# Revit family: 208_S-_ ilmanvaihdon poisto
name_source: partatom
category: Air Terminals
units: mm (PartAtom-declared; Revit-internal decimal feet)

## family parameters
Always vertical = Yes
Cut with Voids When Loaded = No
Part Type = Normal
Room Calculation Point = Yes
Round Connector Dimension = Use Diameter
Shared = No
Work Plane-Based = No

## types (3) — shared parameters
CAT0 = Yes
CL_Location_5000 = 5000 mm  [stored 16.4042 ft]
Description = S-Series roof fans
HT = 3 mm  [stored 0.00984252 ft]
L_ARR = 400 mm  [stored 1.31234 ft]
Manufacturer = Vilpe
QmdConnectorList = 201;D
RR = 50 mm  [stored 0.164042 ft]
URL = http://www.vilpe.com
W_ARR = 400 mm  [stored 1.31234 ft]
XRefLineVPlnId = 7453
YRefLineVPlnId = 7456
magiPartTypeId = 208
magiProductFamilyId = S-* ilmanvaihdon poisto
zero-valued in all types: CLBTZ, H_ARR

## per-type parameters (varying)
| type | C1 | D | H1 | H22 | H81 | LL | R1 | R2 | R6 | R7 | R8 | magiProductId |
| VILPE Ø125S 250x250 EXHAUST VENT | 10 mm  [stored 0.0328084 ft] | 125 mm | 221 mm | 24 mm  [stored 0.0787402 ft] | 28 mm | 125 mm  [stored 0.410105 ft] | 129 mm | 84 mm  [stored 0.275591 ft] | 107 mm | 122 mm | 105 mm  [stored 0.344488 ft] | S-125 ilmanvaihdon poisto |
| VILPE Ø200S 400x400 EXHAUST VENT | 30 mm  [stored 0.0984252 ft] | 200 mm | 370 mm | 37 mm | 46 mm | 198 mm | 200 mm  [stored 0.656168 ft] | 158 mm | 166 mm | 190 mm | 175 mm | S-200 ilmanvaihdon poisto |
| VILPE Ø160S 300x300 EXHAUST VENT | 10 mm  [stored 0.0328084 ft] | 160 mm | 273 mm | 27 mm | 34 mm | 150 mm  [stored 0.492126 ft] | 155 mm | 118 mm | 129 mm | 147 mm | 138 mm | S-160 ilmanvaihdon poisto |

note: column(s) folded — value = type name in every type: MC Product Code

note: [stored X ft] marks values corroborated as IEEE doubles in the binary element streams (Revit-internal decimal feet)

## geometry (parser evidence)
native form markers: Sweep x2
no freeform markers — native parametric forms only
